# Revit family: BLG-95 L
name_source: partatom
category: Generic Models
revit_build: Autodesk Revit 2017 (Build: 20170419_0315(x64)
units: mm (PartAtom-declared; Revit-internal decimal feet)

## family parameters
Always vertical = Yes
Can host rebar = No
Cut with Voids When Loaded = No
Host = Wall
Part Type = Normal
Room Calculation Point = No
Round Connector Dimension = Use Diameter
Shared = No

## types (1)
- BLG-95_L
    Depth = 100 mm  [stored 0.328084 ft]
    EAN = 6430034743132
    Height = 640 mm  [stored 2.09974 ft]
    IP = IP 34
    Keynote = 6120
    LVI = 5282105
    Leveys = 470 mm  [stored 1.54199 ft]
    Manufacturer = Sentakia Oy
    Materiaali = kiillotettu RST
    Model = BLG-95 L
    Sentakia_Material_Default = Stainless Steel, Polished_Sentakia
    Sähkönumero = 8112520
    Teho = 60 W
    URL = http://www.sentakia.com

note: [stored X ft] marks values corroborated as IEEE doubles in the binary element streams (Revit-internal decimal feet)

## geometry (parser evidence)
native form markers: Blend x4, Sweep x7
no freeform markers — native parametric forms only
